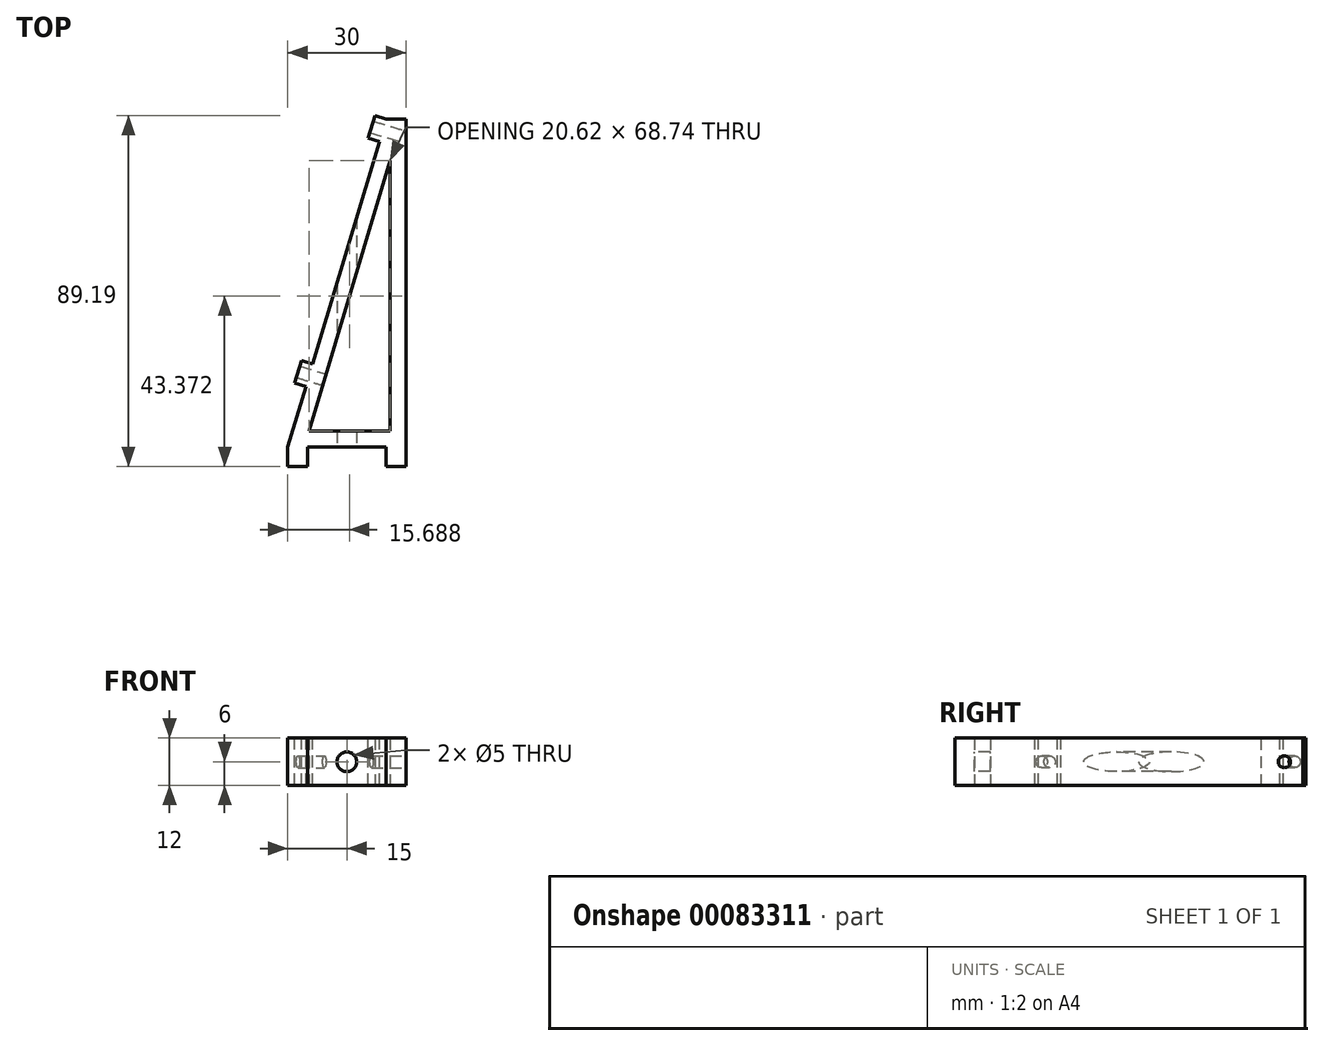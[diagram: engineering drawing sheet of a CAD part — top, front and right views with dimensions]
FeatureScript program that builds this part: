
annotation { "Feature Type Name" : "Feature", "Feature Type Description" : "" }
export const myFeature = defineFeature(function(context is Context, id is Id, definition is map)
    precondition{}
    {
        {
            var Q0;
            Q0=qCreatedBy(makeId("Top.planeOp"),FACE);
            var sketch = newSketch(context, id + "F0", { "sketchPlane" : qUnion([Q0])});
            skLineSegment(sketch, "E0", {"start": v(-20, 0) * mm, "end": v(0, 0) * mm});
            skLineSegment(sketch, "E1", {"start": v(0, 0) * mm, "end": v(0, -5) * mm});
            skLineSegment(sketch, "E2", {"start": v(0, -5) * mm, "end": v(5, -5) * mm});
            skLineSegment(sketch, "E3", {"start": v(5, -5) * mm, "end": v(5, 83.33) * mm});
            skLineSegment(sketch, "E4", {"start": v(-25, 0) * mm, "end": v(-25, -5) * mm});
            skLineSegment(sketch, "E5", {"start": v(-25, -5) * mm, "end": v(-20, -5) * mm});
            skLineSegment(sketch, "E6", {"start": v(-20, -5) * mm, "end": v(-20, 0) * mm});
            skLineSegment(sketch, "E7", {"start": v(5, 83.33) * mm, "end": v(0, 83.33) * mm});
            skLineSegment(sketch, "E8", {"start": v(0, 83.33) * mm, "end": v(-25, 0) * mm});
            skLineSegment(sketch, "E9", {"start": v(-19.62, 4) * mm, "end": v(1, 72.74) * mm});
            skLineSegment(sketch, "E10", {"start": v(1, 72.74) * mm, "end": v(1, 4) * mm});
            skLineSegment(sketch, "E11", {"start": v(1, 4) * mm, "end": v(-19.62, 4) * mm});
            skSolve(sketch);
        }
        {
            var Q0;
            Q0 = qSketchRegion(id + "F0", true);
            extrude(context, id + "F1", {"entities" : qUnion([Q0]), "depth" : 12 * mm});
        }
        {
            var Q0;
            Q0=makeQuery(id+"F1.opExtrude","SWEPT_FACE",FACE,{"disambiguationData":[OSD([sQuery(id+"F0.wireOp",EDGE,"E0")])]});
            var sketch = newSketch(context, id + "F2", { "sketchPlane" : qUnion([Q0])});
            skCircle(sketch, "E12", {"center": v(-10, 6) * mm, "radius": 2.5 * mm});
            skSolve(sketch);
        }
        {
            var Q0;
            Q0 = qSketchRegion(id + "F2", true);
            extrude(context, id + "F3", {"entities" : qUnion([Q0]), "operationType" : NewBodyOperationType.REMOVE, "endBound" : BoundingType.THROUGH_ALL, "oppositeDirection" : true, "depth" : 25 * mm});
        }
        {
            var Q0;
            Q0=makeQuery(id+"F1.opExtrude","SWEPT_FACE",FACE,{"disambiguationData":[OSD([sQuery(id+"F0.wireOp",EDGE,"E8")])]});
            var sketch = newSketch(context, id + "F4", { "sketchPlane" : qUnion([Q0])});
            skLineSegment(sketch, "E13.bottom", {"start": v(-79.82, 0) * mm, "end": v(-73.82, 0) * mm});
            skLineSegment(sketch, "E13.top", {"start": v(-79.82, 12) * mm, "end": v(-73.82, 12) * mm});
            skLineSegment(sketch, "E13.left", {"start": v(-79.82, 0) * mm, "end": v(-79.82, 12) * mm});
            skLineSegment(sketch, "E13.right", {"start": v(-73.82, 0) * mm, "end": v(-73.82, 12) * mm});
            skLineSegment(sketch, "E14.bottom", {"start": v(-14.82, 0) * mm, "end": v(-8.82, 0) * mm});
            skLineSegment(sketch, "E14.top", {"start": v(-14.82, 12) * mm, "end": v(-8.82, 12) * mm});
            skLineSegment(sketch, "E14.left", {"start": v(-14.82, 0) * mm, "end": v(-14.82, 12) * mm});
            skLineSegment(sketch, "E14.right", {"start": v(-8.82, 0) * mm, "end": v(-8.82, 12) * mm});
            skCircle(sketch, "E15", {"center": v(-76.82, 6) * mm, "radius": 1.5 * mm});
            skCircle(sketch, "E16", {"center": v(-11.82, 6) * mm, "radius": 1.5 * mm});
            skPoint(sketch, "E16.centerSnap0", {"position": v(-8.82, 6) * mm});
            skSolve(sketch);
        }
        {
            var Q0;
            Q0=makeQuery(id+"F4.imprint","IMPRINT",FACE,{"disambiguationData":[TD([[makeQuery(id+"F4.imprint","IMPRINT",EDGE,{"derivedFrom":sQuery(id+"F4.wireOp",EDGE,"E13.bottom")}),1.0]])]});
            var Q1;
            Q1=makeQuery(id+"F4.imprint","IMPRINT",FACE,{"disambiguationData":[TD([[makeQuery(id+"F4.imprint","IMPRINT",EDGE,{"derivedFrom":sQuery(id+"F4.wireOp",EDGE,"E14.bottom")}),1.0]])]});
            extrude(context, id + "F5", {"entities" : qUnion([Q0, Q1]), "operationType" : NewBodyOperationType.ADD, "depth" : 3 * mm});
        }
        {
            var Q0;
            Q0=makeQuery(id+"F4.imprint","IMPRINT",FACE,{"disambiguationData":[TD([[makeQuery(id+"F4.imprint","IMPRINT",EDGE,{"derivedFrom":sQuery(id+"F4.wireOp",EDGE,"E15")}),1.0]])]});
            var Q1;
            Q1=makeQuery(id+"F4.imprint","IMPRINT",FACE,{"disambiguationData":[TD([[makeQuery(id+"F4.imprint","IMPRINT",EDGE,{"derivedFrom":sQuery(id+"F4.wireOp",EDGE,"E16")}),1.0]])]});
            extrude(context, id + "F6", {"entities" : qUnion([Q0, Q1]), "operationType" : NewBodyOperationType.REMOVE, "endBound" : BoundingType.UP_TO_NEXT, "oppositeDirection" : true, "depth" : 25 * mm});
        }
    });
